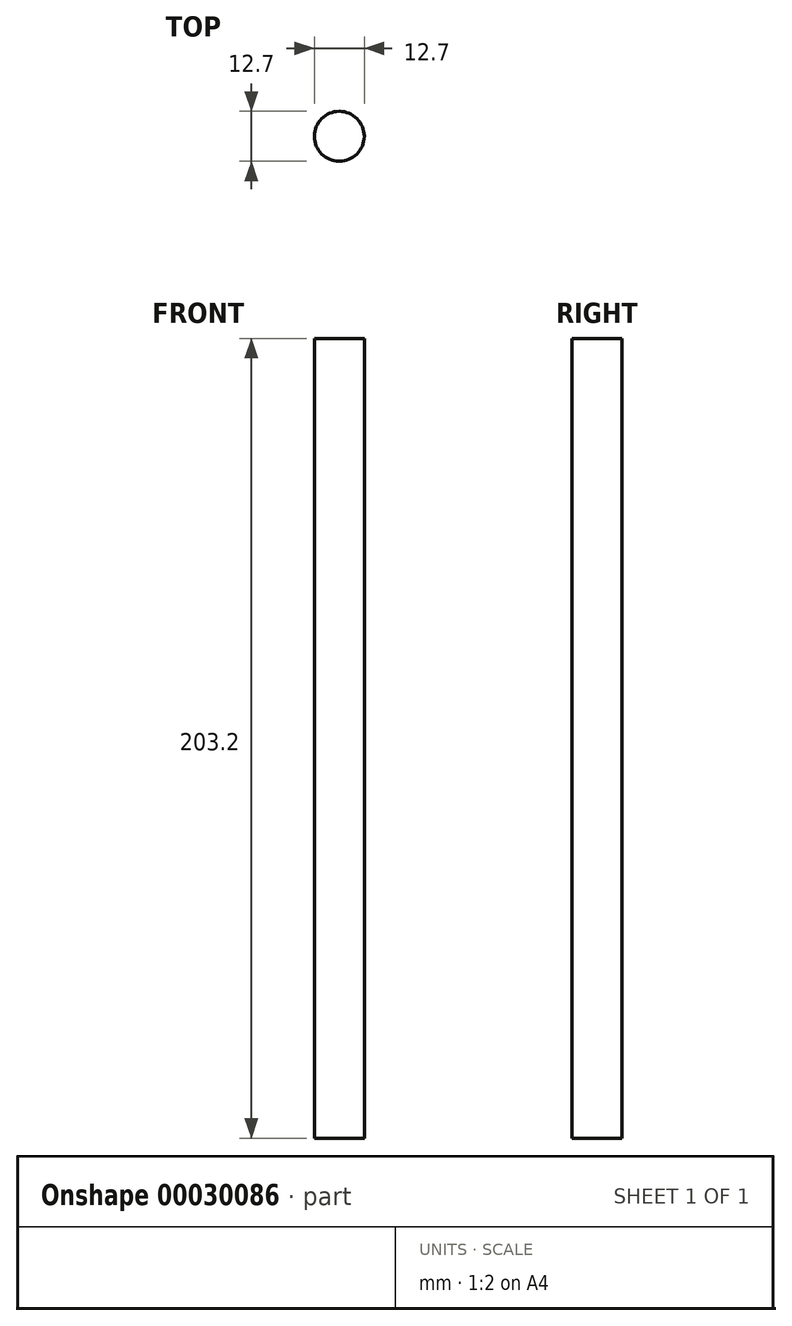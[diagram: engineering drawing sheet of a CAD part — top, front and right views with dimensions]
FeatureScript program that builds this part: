
annotation { "Feature Type Name" : "Feature", "Feature Type Description" : "" }
export const myFeature = defineFeature(function(context is Context, id is Id, definition is map)
    precondition{}
    {
        {
            var Q0;
            Q0=qCreatedBy(makeId("Top.planeOp"),FACE);
            var sketch = newSketch(context, id + "F0", { "sketchPlane" : qUnion([Q0])});
            skCircle(sketch, "E0", {"center": v(0, 0) * mm, "radius": 6.35 * mm});
            skSolve(sketch);
        }
        {
            var Q0;
            Q0 = qSketchRegion(id + "F0", true);
            extrude(context, id + "F1", {"entities" : qUnion([Q0]), "depth" : 203.2 * mm});
        }
    });
